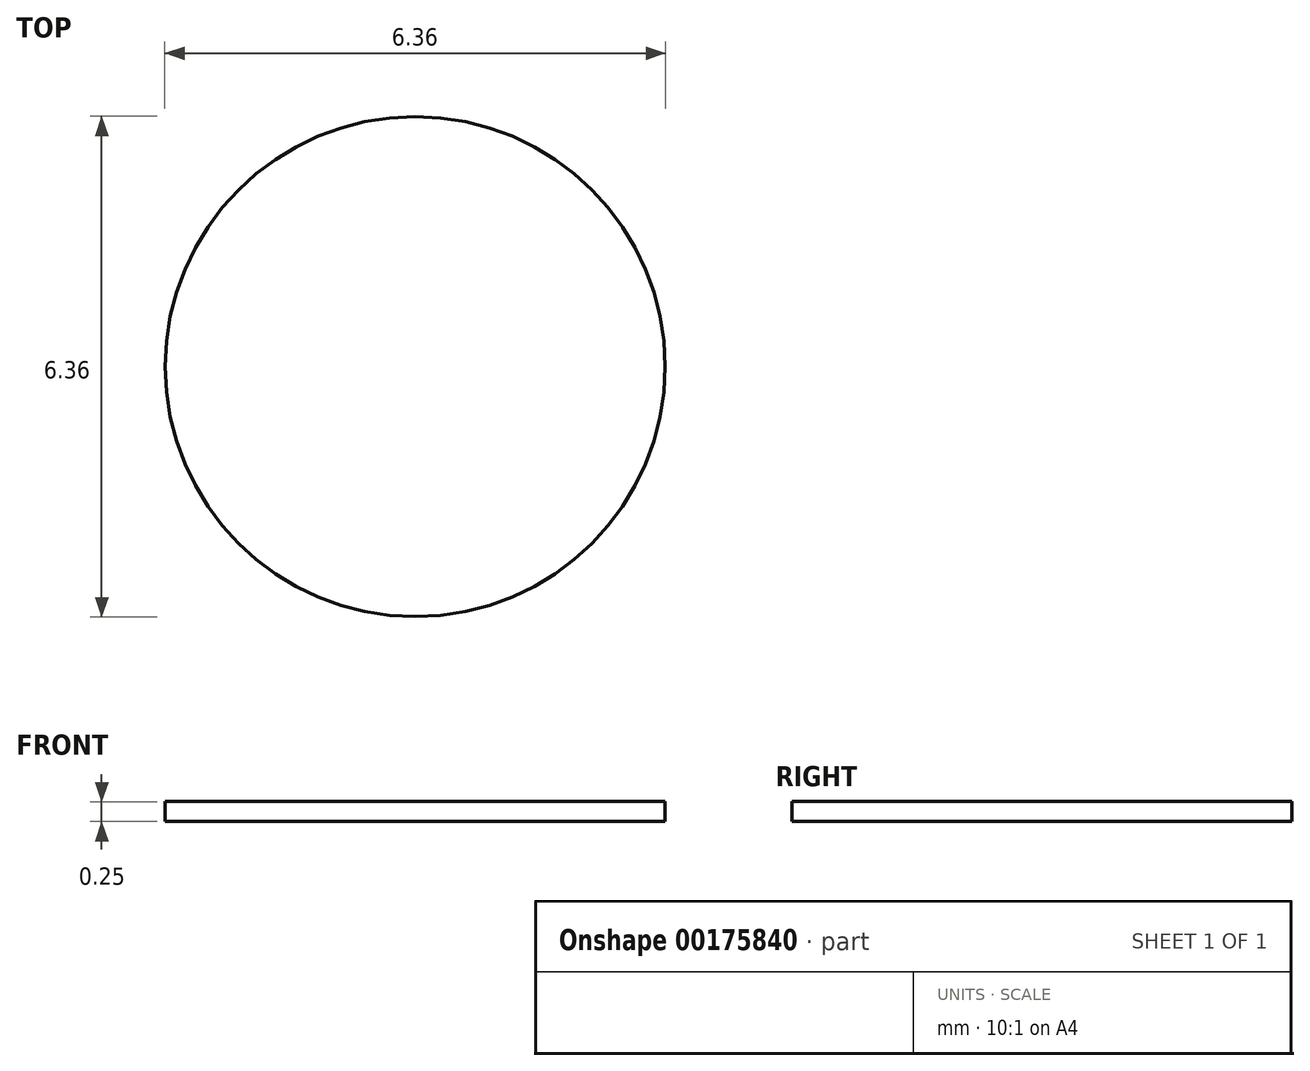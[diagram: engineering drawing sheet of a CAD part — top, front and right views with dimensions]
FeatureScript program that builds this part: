
annotation { "Feature Type Name" : "Feature", "Feature Type Description" : "" }
export const myFeature = defineFeature(function(context is Context, id is Id, definition is map)
    precondition{}
    {
        {
            var Q0;
            Q0=qCreatedBy(makeId("Top.planeOp"),FACE);
            var sketch = newSketch(context, id + "F0", { "sketchPlane" : qUnion([Q0])});
            skCircle(sketch, "E0", {"center": v(0, 0) * mm, "radius": 3.18 * mm});
            skSolve(sketch);
        }
        {
            var Q0;
            Q0 = qSketchRegion(id + "F0", true);
            extrude(context, id + "F1", {"entities" : qUnion([Q0]), "depth" : 0.25 * mm});
        }
    });
